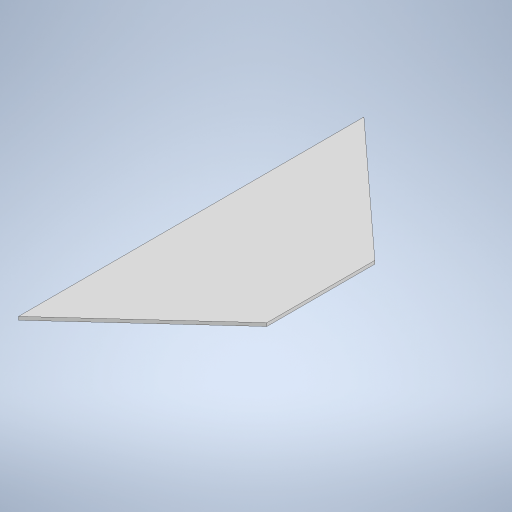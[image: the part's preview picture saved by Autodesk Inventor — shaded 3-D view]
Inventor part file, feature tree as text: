
AUTODESK INVENTOR PART (.ipt)
format: ipt  version: 2024.3 (Build 283343000, 343)  size: 222,720 bytes
history: native  units: mm
features: extrude x1, sketch x1
ambient origin geometry x8: Origin, YZ Plane, XZ Plane, XY Plane, X Axis, Y Axis, Z Axis, Center Point
bodies: Solid1 (feature_tree)
feature tree (2):
  extrude  "Extrusion1"  Depth=3.0mm
  sketch  "Sketch1"  dims[d0=320.0mm d2=100.0mm d3=50.0mm d4=3.0mm d5=0.0mm d6=162.865mm d7=162.865mm]
